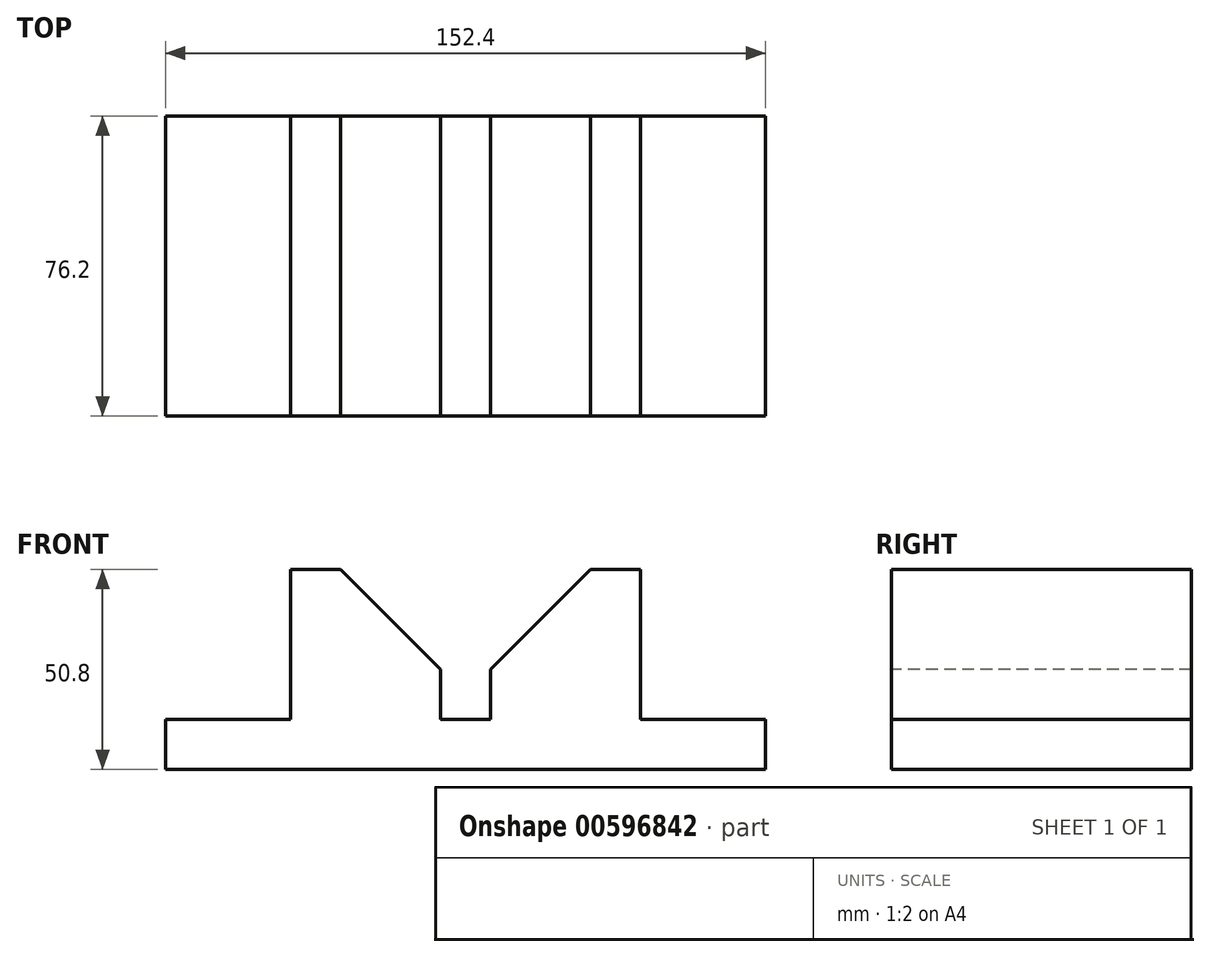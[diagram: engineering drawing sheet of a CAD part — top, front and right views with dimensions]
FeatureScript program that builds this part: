
annotation { "Feature Type Name" : "Feature", "Feature Type Description" : "" }
export const myFeature = defineFeature(function(context is Context, id is Id, definition is map)
    precondition{}
    {
        {
            var Q0;
            Q0=qCreatedBy(makeId("Front.planeOp"),FACE);
            var sketch = newSketch(context, id + "F0", { "sketchPlane" : qUnion([Q0])});
            skLineSegment(sketch, "E0", {"start": v(0, 0) * mm, "end": v(0, 12.7) * mm});
            skLineSegment(sketch, "E1", {"start": v(0, 12.7) * mm, "end": v(31.75, 12.7) * mm});
            skLineSegment(sketch, "E2", {"start": v(31.75, 12.7) * mm, "end": v(31.75, 50.8) * mm});
            skLineSegment(sketch, "E3", {"start": v(31.75, 50.8) * mm, "end": v(44.45, 50.8) * mm});
            skLineSegment(sketch, "E4", {"start": v(44.45, 50.8) * mm, "end": v(69.85, 25.4) * mm});
            skLineSegment(sketch, "E5", {"start": v(69.85, 25.4) * mm, "end": v(69.85, 12.7) * mm});
            skLineSegment(sketch, "E6", {"start": v(69.85, 12.7) * mm, "end": v(82.55, 12.7) * mm});
            skLineSegment(sketch, "E7", {"start": v(82.55, 12.7) * mm, "end": v(82.55, 25.4) * mm});
            skLineSegment(sketch, "E8", {"start": v(82.55, 25.4) * mm, "end": v(107.95, 50.8) * mm});
            skLineSegment(sketch, "E9", {"start": v(107.95, 50.8) * mm, "end": v(120.65, 50.8) * mm});
            skLineSegment(sketch, "E10", {"start": v(120.65, 50.8) * mm, "end": v(120.65, 12.7) * mm});
            skLineSegment(sketch, "E11", {"start": v(120.65, 12.7) * mm, "end": v(152.4, 12.7) * mm});
            skLineSegment(sketch, "E12", {"start": v(152.4, 12.7) * mm, "end": v(152.4, 0) * mm});
            skLineSegment(sketch, "E13", {"start": v(152.4, 0) * mm, "end": v(0, 0) * mm});
            skSolve(sketch);
        }
        {
            var Q0;
            Q0=makeQuery(id+"F0.imprint","IMPRINT",FACE,{"disambiguationData":[TD([[makeQuery(id+"F0.imprint","IMPRINT",EDGE,{"derivedFrom":sQuery(id+"F0.wireOp",EDGE,"E0")}),-1.0]])]});
            extrude(context, id + "F1", {"entities" : qUnion([Q0]), "oppositeDirection" : true, "depth" : 76.2 * mm, "offsetDistance" : 25.4 * mm});
        }
    });
